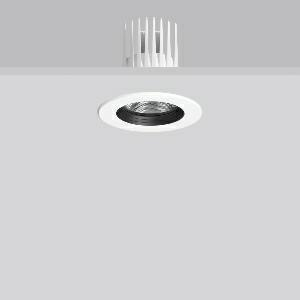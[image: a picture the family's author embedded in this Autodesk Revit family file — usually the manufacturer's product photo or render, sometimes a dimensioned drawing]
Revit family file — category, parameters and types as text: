
# Revit family: heledon_mini_e_901741_002_3_76_61d3
name_source: partatom
category: Lighting Fixtures
units: mm (PartAtom-declared; Revit-internal decimal feet)

## family parameters
Cut with Voids When Loaded = No
Host = Face
Light Source = No
Part Type = Normal
Room Calculation Point = No
Round Connector Dimension = Use Diameter
Shared = No

## types (1)
- HELEDON mini E (1 x LED Modul 935, 2500 lm, 3500)
    Apparent Load = 20 VA
    Approval mark = CE
    CIE Flux Codes = 99 100 100 100 100
    Color Rendering = 92
    Color Temperature = 3500
    Default Elevation = 1800 mm
    Description = Series: HELEDON mini
Round recessed downlight. Housing: die-cast aluminium, powder-coated. Black plastic ring and recessed LED to prevent glare from the side. Optical assembly with reflector made of MIRO-Silver with 98% total light reflection for outstanding efficiency - can be changed without tools. Best colour rendering index Ra>90. Suitable for Recessed ceiling mounting. Installation without tools thanks to spring fastening system. Including separate LED converter with connecting cable 600 mm.High quality converter without flickering and stroboscopic effect. Through-wiring box (5 pole) available as accessory. The following accessories can be mounted without use of tools: interchangeable lenses, decorative glasses, honeycomb louvre, clear and frosted diffusers, white interchangeable plastic ring. 
Colour: traffic white, matt (RAL 9016)
Diameter: 124 mm
Height: 3 mm
Cut-out diameter: 114 mm
Recess height: 170 mm
Luminaire: recess height: 120 mm
Lamp: LED
Socket: without socket
Colour temperature: 3500K
Colour rendering index (CRI): 92
System power: 20 W
Rated luminous flux: 2500 lm
Luminous efficiency: 125 lm/W
Control gear: Converter, dimmable, DALI
Protection class: II
Type of protection: IP 20
    Height = 0 mm  [stored 0 ft]
    Lamp = 1 x LED Modul 935
    Lamp Light Flux = 2500 lm
    Lamp count = 1
    Length = 124 mm  [stored 0.406824 ft]
    Lifetime = 50000 h
    Luminous efficacy = 125 lm/W
    Manufacturer = RZB
    ModVariant = No
    Model = 901741.002.3.76
    Mounting Place = Ceiling
    Mounting Type = Recessed
    Number of Poles = 1
    OnlyDefault = Yes
    Power Factor = 1
    Product Name = HELEDON mini E
    Product group = Recessed downlights
    ProductGroupID = 402
    Protection Class = Protection class II
    Protection Degree = IP 20
    RLX_Detail_Level = 1
    RLX_Emergency_Light_Flux = 0 lm
    RLX_Emergency_Type = 0
    RLX_Emergency_Type_DB = No
    RlxData = <blob elided: 126893 chars, md5=1b8ddea7>
    Socket = socket
    Standby Power = 0 W
    System Light Flux = 2500 lm
    System Power = 20 W
    Type Comments = Product without accessories
    Type Image = 901657.002.jpg
    URL = http://relux.com
    VarID = ---
    Voltage = 230 V
    Voltage Range = 220-240 V
    Weight = 0.00 kg
    Width = 0 mm  [stored 0 ft]

note: [stored X ft] marks values corroborated as IEEE doubles in the binary element streams (Revit-internal decimal feet)

## geometry (parser evidence)
native form markers: Blend x4, Sweep x11
no freeform markers — native parametric forms only
